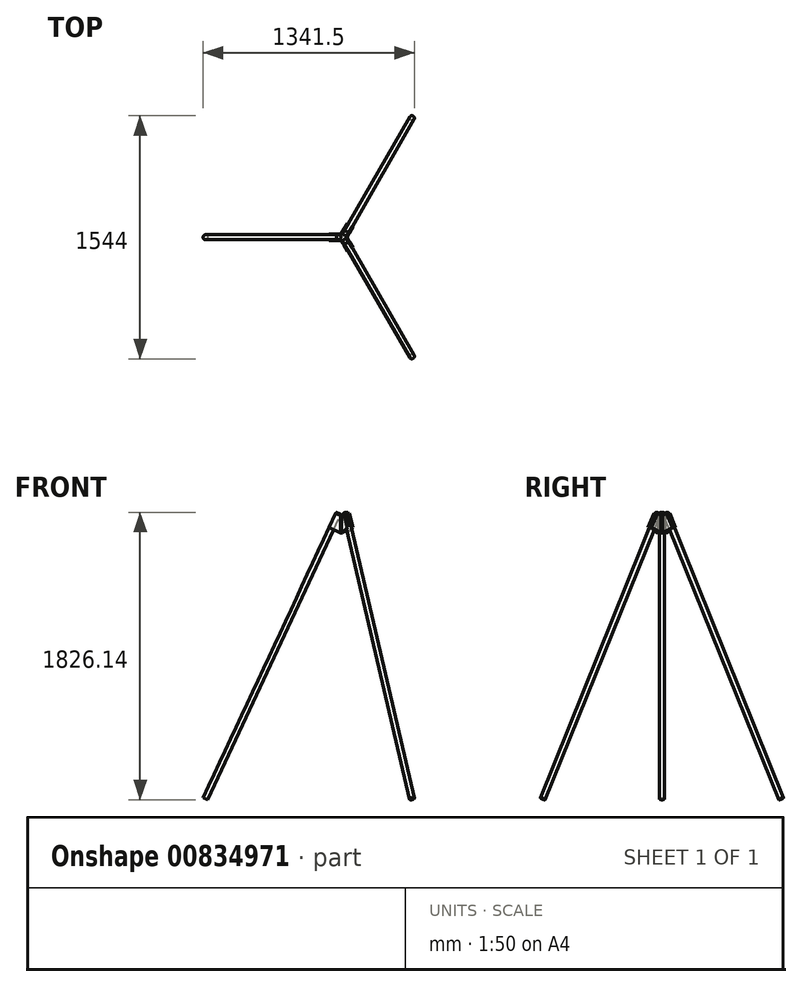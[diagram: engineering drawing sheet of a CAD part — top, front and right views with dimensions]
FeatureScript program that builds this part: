
annotation { "Feature Type Name" : "Feature", "Feature Type Description" : "" }
export const myFeature = defineFeature(function(context is Context, id is Id, definition is map)
    precondition{}
    {
        {
            assignVariable(context, id + "F0", {"variableType" : VariableType.LENGTH, "name" : "PipeDia", "lengthValue" : 32 * mm});
        }
        {
            assignVariable(context, id + "F1", {"variableType" : VariableType.LENGTH, "name" : "PipeLength", "lengthValue" : 2000 * mm});
        }
        {
            assignVariable(context, id + "F2", {"variableType" : VariableType.ANGLE, "name" : "LegAngle", "angleValue" : 25 * degree});
        }
        {
            var Q0;
            Q0=qCreatedBy(makeId("Right.planeOp"),FACE);
            var sketch = newSketch(context, id + "F3", { "sketchPlane" : qUnion([Q0])});
            skLineSegment(sketch, "E0", {"start": v(0, 0) * mm, "end": v(-174.54, 0) * mm, "construction": true});
            skLineSegment(sketch, "E1", {"start": v(0, 0) * mm, "end": v(0, 119.44) * mm, "construction": true});
            skSolve(sketch);
        }
        {
            var Q0;
            Q0=sQuery(id+"F3.wireOp",EDGE,"E0");
            var Q1;
            Q1=sQuery(id+"F3.wireOp",VERTEX,"E1.end");
            cPlane(context, id + "F4", {"entities" : qUnion([Q0, Q1]), "cplaneType" : CPlaneType.LINE_ANGLE, "offset" : 25 * mm, "angle" : 90 * degree - getVariable(context, 'LegAngle'), "width" : 150 * mm, "height" : 150 * mm});
        }
        {
            var Q0;
            Q0=qCreatedBy(id+"F4.planeOp",FACE);
            var sketch = newSketch(context, id + "F5", { "sketchPlane" : qUnion([Q0])});
            skCircle(sketch, "E2", {"center": v(-32, 0) * mm, "radius": 16 * mm});
            skSolve(sketch);
        }
        {
            var Q0;
            Q0=qSketchRegion(id+"F5",true);
            extrude(context, id + "F6", {"entities" : qUnion([Q0]), "depth" : getVariable(context, 'PipeLength'), "offsetDistance" : 25 * mm});
        }
        {
            var Q0;
            Q0=makeQuery(id+"F6.opExtrude","SWEPT_BODY",BODY,{"disambiguationData":[OSD([sQuery(id+"F5.wireOp",EDGE,"E2")])]});
            var Q1;
            Q1=sQuery(id+"F3.wireOp",EDGE,"E1");
            circularPattern(context, id + "F7", {"entities" : qUnion([Q0]), "axis" : qUnion([Q1]), "angle" : 360 * degree, "instanceCount" : 3, "equalSpace" : true});
        }
        {
            var Q0;
            Q0=makeQuery(id+"F7.opPattern","COPY",FACE,{"derivedFrom":makeQuery(id+"F6.opExtrude","CAP_FACE",FACE,{"disambiguationData":[OSD([sQuery(id+"F5.wireOp",EDGE,"E2")])],"isStart":true}),"instanceName":"1"});
            var sketch = newSketch(context, id + "F8", { "sketchPlane" : qUnion([Q0])});
            skCircle(sketch, "E3.0.0", {"center": v(14.84, -28.35) * mm, "radius": 16 * mm});
            skSolve(sketch);
        }
        {
            var Q0;
            Q0=makeQuery(id+"F7.opPattern","COPY",FACE,{"derivedFrom":makeQuery(id+"F6.opExtrude","CAP_FACE",FACE,{"disambiguationData":[OSD([sQuery(id+"F5.wireOp",EDGE,"E2")])],"isStart":true}),"instanceName":"2"});
            var sketch = newSketch(context, id + "F9", { "sketchPlane" : qUnion([Q0])});
            skCircle(sketch, "E4.0.0", {"center": v(14.84, 28.35) * mm, "radius": 16 * mm});
            skSolve(sketch);
        }
        {
            var Q0;
            Q0=makeQuery(id+"F7.opPattern","COPY",FACE,{"derivedFrom":makeQuery(id+"F6.opExtrude","CAP_FACE",FACE,{"disambiguationData":[OSD([sQuery(id+"F5.wireOp",EDGE,"E2")])],"isStart":false}),"instanceName":"2"});
            var sketch = newSketch(context, id + "F10", { "sketchPlane" : qUnion([Q0])});
            skCircle(sketch, "E5.0.0", {"center": v(14.84, -28.35) * mm, "radius": 16 * mm});
            skSolve(sketch);
        }
        {
            var Q0;
            Q0=sQuery(id+"F10.wireOp",VERTEX,"E5.0.0.center");
            var Q1;
            Q1=sQuery(id+"F9.wireOp",VERTEX,"E4.0.0.center");
            var Q2;
            Q2=sQuery(id+"F8.wireOp",VERTEX,"E3.0.0.center");
            cPlane(context, id + "F11", {"entities" : qUnion([Q0, Q1, Q2]), "cplaneType" : CPlaneType.THREE_POINT, "offset" : 25 * mm, "width" : 150 * mm, "height" : 150 * mm});
        }
        {
            var Q0;
            Q0=sQuery(id+"F10.wireOp",VERTEX,"E5.0.0.center");
            var Q1;
            Q1=sQuery(id+"F9.wireOp",VERTEX,"E4.0.0.center");
            var Q2;
            Q2=sQuery(id+"F3.wireOp",VERTEX,"E0.start");
            cPlane(context, id + "F12", {"entities" : qUnion([Q0, Q1, Q2]), "cplaneType" : CPlaneType.THREE_POINT, "offset" : 25 * mm, "width" : 150 * mm, "height" : 150 * mm});
        }
        {
            var Q0;
            Q0=qCreatedBy(id+"F12.planeOp",FACE);
            cPlane(context, id + "F13", {"entities" : qUnion([Q0]), "cplaneType" : CPlaneType.OFFSET, "offset" : getVariable(context, 'PipeDia') / 2, "width" : 150 * mm, "height" : 150 * mm});
        }
        {
            var Q0;
            Q0=qCreatedBy(id+"F13.planeOp",FACE);
            var sketch = newSketch(context, id + "F14", { "sketchPlane" : qUnion([Q0])});
            skLineSegment(sketch, "E6", {"start": v(-17.65, 0) * mm, "end": v(-46.66, 13.52) * mm});
            skLineSegment(sketch, "E7", {"start": v(-46.66, 13.52) * mm, "end": v(-88.92, -77.1) * mm});
            skLineSegment(sketch, "E8", {"start": v(-88.92, -77.1) * mm, "end": v(-17.65, -110.34) * mm});
            skLineSegment(sketch, "E9", {"start": v(-17.65, -110.34) * mm, "end": v(-17.65, 0) * mm});
            skLineSegment(sketch, "E10", {"start": v(-888.74, -1792.33) * mm, "end": v(-43.5, 20.29) * mm, "construction": true});
            skLineSegment(sketch, "E11", {"start": v(-14.5, 6.76) * mm, "end": v(-859.74, -1805.85) * mm});
            skSolve(sketch);
        }
        {
            var Q0;
            Q0 = qSketchRegion(id + "F14", true);
            extrude(context, id + "F15", {"entities" : qUnion([Q0]), "depth" : 5 * mm, "offsetDistance" : 25 * mm});
        }
        {
            var Q0;
            Q0=makeQuery(id+"F15.opExtrude","SWEPT_BODY",BODY,{"disambiguationData":[OSD([sQuery(id+"F14.wireOp",EDGE,"E6"),sQuery(id+"F14.wireOp",EDGE,"E7"),sQuery(id+"F14.wireOp",EDGE,"E8"),sQuery(id+"F14.wireOp",EDGE,"E9")])]});
            var Q1;
            Q1=qCreatedBy(id+"F12.planeOp",FACE);
            mirror(context, id + "F16", {"entities" : qUnion([Q0]), "mirrorPlane" : qUnion([Q1])});
        }
        {
            var Q0;
            Q0=makeQuery(id+"F16.opPattern","COPY",BODY,{"derivedFrom":makeQuery(id+"F15.opExtrude","SWEPT_BODY",BODY,{"disambiguationData":[OSD([sQuery(id+"F14.wireOp",EDGE,"E6"),sQuery(id+"F14.wireOp",EDGE,"E7"),sQuery(id+"F14.wireOp",EDGE,"E8"),sQuery(id+"F14.wireOp",EDGE,"E9")])]}),"instanceName":"1"});
            var Q1;
            Q1=makeQuery(id+"F15.opExtrude","SWEPT_BODY",BODY,{"disambiguationData":[OSD([sQuery(id+"F14.wireOp",EDGE,"E6"),sQuery(id+"F14.wireOp",EDGE,"E7"),sQuery(id+"F14.wireOp",EDGE,"E8"),sQuery(id+"F14.wireOp",EDGE,"E9")])]});
            var Q2;
            Q2=sQuery(id+"F3.wireOp",EDGE,"E1");
            circularPattern(context, id + "F17", {"entities" : qUnion([Q0, Q1]), "axis" : qUnion([Q2]), "angle" : 360 * degree, "instanceCount" : 3, "equalSpace" : true});
        }
        {
            var Q0;
            Q0=makeQuery(id+"F15.opExtrude","CAP_VERTEX",VERTEX,{"disambiguationData":[OSD([sQuery(id+"F14.wireOp",EDGE,"E6"),sQuery(id+"F14.wireOp",EDGE,"E9"),sQuery(id+"F14.wireOp",EDGE,"E11")])],"isStart":false});
            var Q1;
            Q1=makeQuery(id+"F17.opPattern","COPY",VERTEX,{"derivedFrom":makeQuery(id+"F16.opPattern","COPY",VERTEX,{"derivedFrom":makeQuery(id+"F15.opExtrude","CAP_VERTEX",VERTEX,{"disambiguationData":[OSD([sQuery(id+"F14.wireOp",EDGE,"E6"),sQuery(id+"F14.wireOp",EDGE,"E9"),sQuery(id+"F14.wireOp",EDGE,"E11")])],"isStart":false}),"instanceName":"1"}),"instanceName":"1"});
            var Q2;
            Q2=makeQuery(id+"F17.opPattern","COPY",VERTEX,{"derivedFrom":makeQuery(id+"F16.opPattern","COPY",VERTEX,{"derivedFrom":makeQuery(id+"F15.opExtrude","CAP_VERTEX",VERTEX,{"disambiguationData":[OSD([sQuery(id+"F14.wireOp",EDGE,"E6"),sQuery(id+"F14.wireOp",EDGE,"E9"),sQuery(id+"F14.wireOp",EDGE,"E11")])],"isStart":false}),"instanceName":"1"}),"instanceName":"2"});
            cPlane(context, id + "F18", {"entities" : qUnion([Q0, Q1, Q2]), "cplaneType" : CPlaneType.THREE_POINT, "offset" : 25 * mm, "width" : 150 * mm, "height" : 150 * mm});
        }
        {
            var Q0;
            Q0=qCreatedBy(id+"F18.planeOp",FACE);
            var sketch = newSketch(context, id + "F19", { "sketchPlane" : qUnion([Q0])});
            skLineSegment(sketch, "E12", {"start": v(-9.36, -25.79) * mm, "end": v(-17.65, -21) * mm});
            skLineSegment(sketch, "E13", {"start": v(-17.65, -21) * mm, "end": v(-17.65, -16) * mm});
            skLineSegment(sketch, "E14", {"start": v(-17.65, -16) * mm, "end": v(-5.03, -23.29) * mm});
            skLineSegment(sketch, "E15", {"start": v(-5.03, -23.29) * mm, "end": v(-9.36, -25.79) * mm});
            skSolve(sketch);
        }
        {
            var Q0;
            Q0 = qSketchRegion(id + "F19", true);
            var Q1;
            Q1=makeQuery(id+"F15.opExtrude","CAP_VERTEX",VERTEX,{"disambiguationData":[OSD([sQuery(id+"F14.wireOp",EDGE,"E8"),sQuery(id+"F14.wireOp",EDGE,"E9")])],"isStart":false});
            extrude(context, id + "F20", {"entities" : qUnion([Q0]), "endBound" : BoundingType.UP_TO_VERTEX, "depth" : 25 * mm, "endBoundEntityVertex" : qUnion([Q1]), "offsetDistance" : 25 * mm});
        }
        {
            var Q0;
            Q0=makeQuery(id+"F20.opExtrude","SWEPT_BODY",BODY,{"disambiguationData":[OSD([sQuery(id+"F19.wireOp",EDGE,"E12"),sQuery(id+"F19.wireOp",EDGE,"E13"),sQuery(id+"F19.wireOp",EDGE,"E14"),sQuery(id+"F19.wireOp",EDGE,"E15")])]});
            var Q1;
            Q1=sQuery(id+"F3.wireOp",EDGE,"E1");
            circularPattern(context, id + "F21", {"entities" : qUnion([Q0]), "axis" : qUnion([Q1]), "angle" : 360 * degree, "instanceCount" : 3, "equalSpace" : true});
        }
    });
